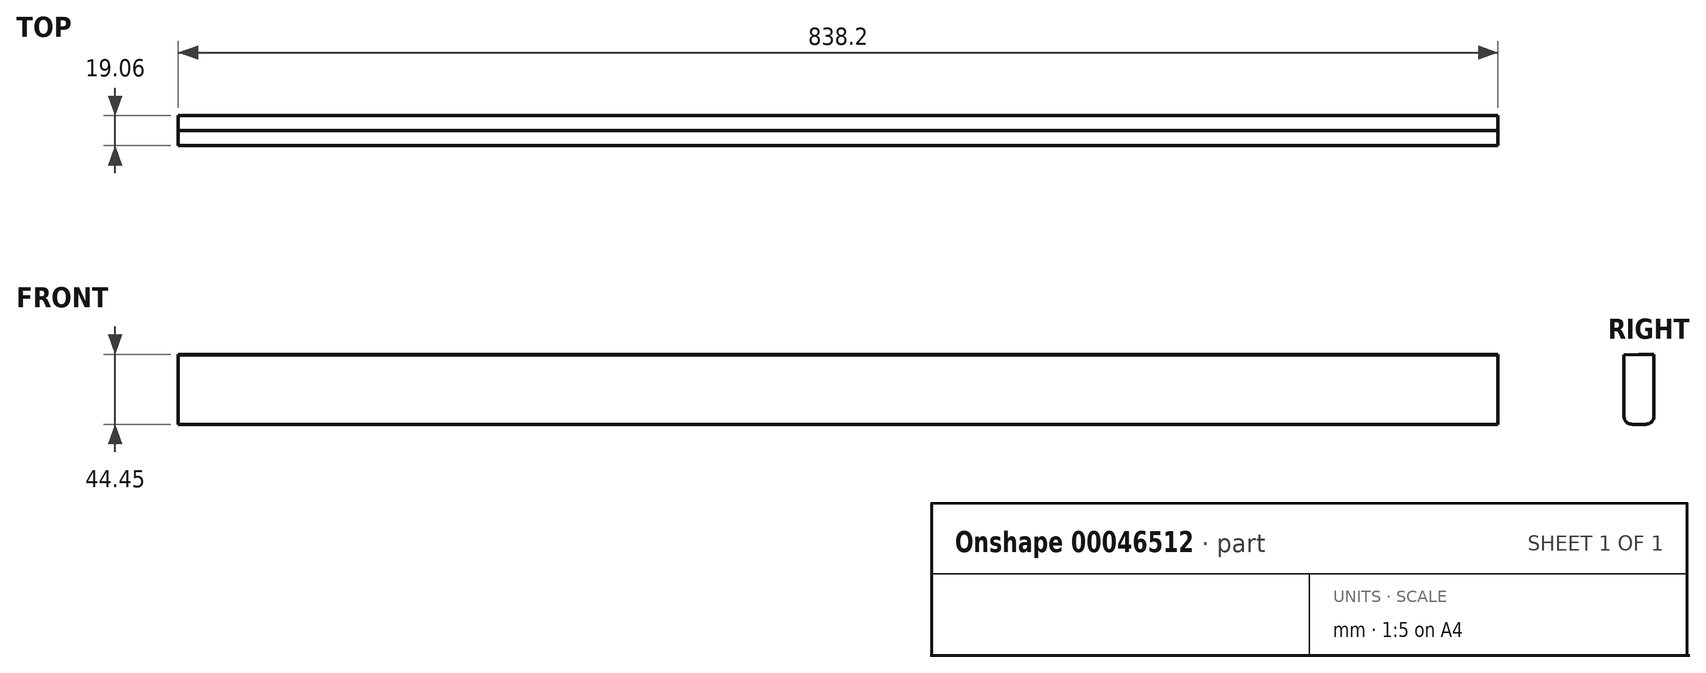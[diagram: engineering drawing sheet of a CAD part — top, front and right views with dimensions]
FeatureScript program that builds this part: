
annotation { "Feature Type Name" : "Feature", "Feature Type Description" : "" }
export const myFeature = defineFeature(function(context is Context, id is Id, definition is map)
    precondition{}
    {
        {
            var Q0;
            Q0=qCreatedBy(makeId("Right.planeOp"),FACE);
            var sketch = newSketch(context, id + "F0", { "sketchPlane" : qUnion([Q0])});
            skLineSegment(sketch, "E0", {"start": v(-9.52, -18.36) * mm, "end": v(9.53, -18.36) * mm});
            skLineSegment(sketch, "E1", {"start": v(9.53, -18.36) * mm, "end": v(9.53, 26.1) * mm});
            skLineSegment(sketch, "E2", {"start": v(9.53, 26.1) * mm, "end": v(0, 26.1) * mm});
            skLineSegment(sketch, "E3", {"start": v(0, 26.1) * mm, "end": v(-9.52, 25.57) * mm});
            skLineSegment(sketch, "E4", {"start": v(-9.52, 25.57) * mm, "end": v(-9.52, -18.36) * mm});
            skSolve(sketch);
        }
        {
            var Q0;
            Q0=makeQuery(id+"F0.imprint","IMPRINT",FACE,{"disambiguationData":[TD([[makeQuery(id+"F0.imprint","IMPRINT",EDGE,{"derivedFrom":sQuery(id+"F0.wireOp",EDGE,"E0")}),1.0]])]});
            extrude(context, id + "F1", {"entities" : qUnion([Q0]), "depth" : 419.1 * mm, "hasSecondDirection" : true, "secondDirectionOppositeDirection" : true, "secondDirectionDepth" : 419.1 * mm});
        }
        {
            var Q0;
            Q0=makeQuery(id+"F1.opExtrude","SWEPT_EDGE",EDGE,{"disambiguationData":[OSD([sQuery(id+"F0.wireOp",EDGE,"E0"),sQuery(id+"F0.wireOp",EDGE,"E4")])]});
            var Q1;
            Q1=makeQuery(id+"F1.opExtrude","SWEPT_EDGE",EDGE,{"disambiguationData":[OSD([sQuery(id+"F0.wireOp",EDGE,"E0"),sQuery(id+"F0.wireOp",EDGE,"E1")])]});
            fillet(context, id + "F2", {"entities" : qUnion([Q0, Q1]), "radius" : 5.08 * mm, "tangentPropagation" : true, "allowEdgeOverflow" : false});
        }
    });
